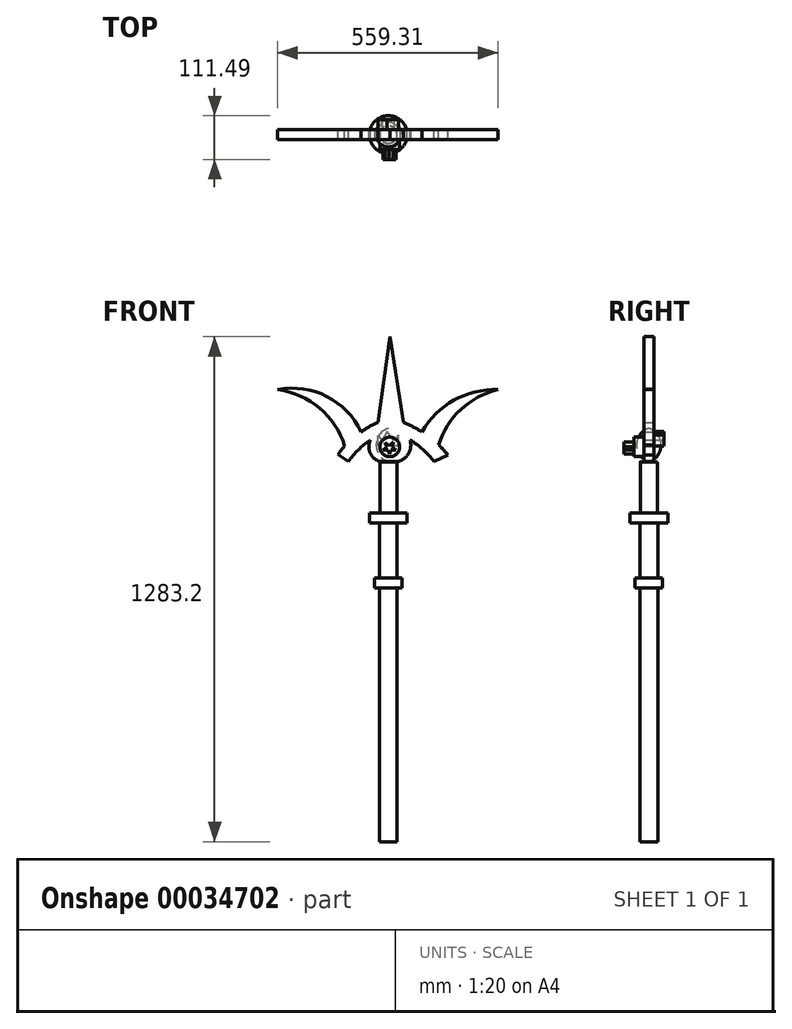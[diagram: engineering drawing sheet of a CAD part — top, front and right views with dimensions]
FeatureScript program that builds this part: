
annotation { "Feature Type Name" : "Feature", "Feature Type Description" : "" }
export const myFeature = defineFeature(function(context is Context, id is Id, definition is map)
    precondition{}
    {
        {
            var Q0;
            Q0=qCreatedBy(makeId("Front.planeOp"),FACE);
            var sketch = newSketch(context, id + "F0", { "sketchPlane" : qUnion([Q0])});
            skLineSegment(sketch, "E0.top", {"start": v(-65.68, 492.37) * mm, "end": v(-22.5, 492.37) * mm});
            skArc(sketch, "E1", {"start": v(-44.09, 492.37) * mm, "mid": v(-0.15, 503.17) * mm, "end": v(11.1, 547) * mm});
            skArc(sketch, "E2", {"start": v(-89.66, 546.65) * mm, "mid": v(-84.3, 504.88) * mm, "end": v(-44.09, 492.37) * mm});
            skArc(sketch, "E3", {"start": v(72.25, 492.37) * mm, "mid": v(20.55, 541) * mm, "end": v(-44.09, 570.32) * mm});
            skArc(sketch, "E4", {"start": v(-44.09, 570.32) * mm, "mid": v(-100.63, 538.76) * mm, "end": v(-145.8, 492.37) * mm});
            skLineSegment(sketch, "E5", {"start": v(72.25, 492.37) * mm, "end": v(107.25, 508.86) * mm});
            skLineSegment(sketch, "E6", {"start": v(-145.8, 492.37) * mm, "end": v(-171.5, 510.6) * mm});
            skArc(sketch, "E7", {"start": v(-40.37, 602.27) * mm, "mid": v(-113.68, 567.51) * mm, "end": v(-171.5, 510.6) * mm});
            skArc(sketch, "E8", {"start": v(107.25, 508.86) * mm, "mid": v(41.18, 567.81) * mm, "end": v(-40.37, 602.27) * mm});
            skArc(sketch, "E9", {"start": v(-154.84, 531.2) * mm, "mid": v(-218.84, 628.04) * mm, "end": v(-325.09, 674.82) * mm});
            skArc(sketch, "E10", {"start": v(-113.68, 567.51) * mm, "mid": v(-200.67, 658.03) * mm, "end": v(-325.09, 674.82) * mm});
            skArc(sketch, "E11", {"start": v(234.22, 674.82) * mm, "mid": v(140.25, 624.74) * mm, "end": v(83.74, 534.5) * mm});
            skArc(sketch, "E12", {"start": v(234.22, 674.82) * mm, "mid": v(122.84, 648.12) * mm, "end": v(41.18, 567.81) * mm});
            skLineSegment(sketch, "E13", {"start": v(-70.87, 591.42) * mm, "end": v(-40.37, 809.45) * mm});
            skLineSegment(sketch, "E14", {"start": v(-40.37, 809.45) * mm, "end": v(-5.06, 591.2) * mm});
            skLineSegment(sketch, "E15", {"start": v(-44.09, 492.37) * mm, "end": v(-44.09, -473.75) * mm});
            skLineSegment(sketch, "E16", {"start": v(-22.5, 492.37) * mm, "end": v(-22.5, 361.02) * mm});
            skLineSegment(sketch, "E17", {"start": v(-22.5, 361.02) * mm, "end": v(3.9, 361.02) * mm});
            skLineSegment(sketch, "E18", {"start": v(3.9, 361.02) * mm, "end": v(3.9, 335.62) * mm});
            skLineSegment(sketch, "E19", {"start": v(3.9, 335.62) * mm, "end": v(-21.5, 335.62) * mm});
            skLineSegment(sketch, "E20", {"start": v(-21.5, 335.62) * mm, "end": v(-21.5, 196.28) * mm});
            skLineSegment(sketch, "E21", {"start": v(-21.5, 196.28) * mm, "end": v(-8.8, 196.28) * mm});
            skLineSegment(sketch, "E22", {"start": v(-8.8, 196.28) * mm, "end": v(-8.8, 170.88) * mm});
            skLineSegment(sketch, "E23", {"start": v(-8.8, 170.88) * mm, "end": v(-21.5, 170.88) * mm});
            skLineSegment(sketch, "E24", {"start": v(-21.5, 170.88) * mm, "end": v(-21.5, -473.75) * mm});
            skLineSegment(sketch, "E25", {"start": v(-21.5, -473.75) * mm, "end": v(-44.09, -473.75) * mm});
            skSolve(sketch);
        }
        {
            var Q0;
            {var subQ1=sQuery(id+"F0.wireOp",EDGE,"E15");Q0=makeQuery(id+"F0.imprint","IMPRINT",FACE,{"disambiguationData":[TD([[makeQuery(id+"F0.imprint","IMPRINT",EDGE,{"derivedFrom":subQ1}),1.0]])]});}
            var Q1;
            Q1=sQuery(id+"F0.wireOp",EDGE,"E15");
            revolve(context, id + "F1", {"entities" : qUnion([Q0]), "axis" : qUnion([Q1]), "revolveType" : RevolveType.FULL});
        }
        {
            var Q0;
            {var subQ0=sQuery(id+"F0.wireOp",EDGE,"E3");var subQ3=sQuery(id+"F0.wireOp",EDGE,"E1");var subQ4=makeQuery(id+"F0.imprint","INTERSECT",VERTEX,{"derivedFrom":[subQ3,subQ0]});Q0=makeQuery(id+"F0.imprint","IMPRINT",FACE,{"disambiguationData":[TD([[makeQuery(id+"F0.imprint","IMPRINT",EDGE,{"disambiguationData":[TD([[subQ4,1.0]])],"derivedFrom":subQ3}),1.0]])]});}
            extrude(context, id + "F2", {"entities" : qUnion([Q0]), "endBound" : BoundingType.SYMMETRIC, "depth" : 25.4 * mm});
        }
        {
            var Q0;
            {var subQ1=sQuery(id+"F0.wireOp",EDGE,"E9");Q0=makeQuery(id+"F0.imprint","IMPRINT",FACE,{"disambiguationData":[TD([[makeQuery(id+"F0.imprint","IMPRINT",EDGE,{"derivedFrom":subQ1}),-1.0]])]});}
            var Q1;
            {var subQ1=sQuery(id+"F0.wireOp",EDGE,"E13");Q1=makeQuery(id+"F0.imprint","IMPRINT",FACE,{"disambiguationData":[TD([[makeQuery(id+"F0.imprint","IMPRINT",EDGE,{"derivedFrom":subQ1}),-1.0]])]});}
            var Q2;
            {var subQ0=sQuery(id+"F0.wireOp",EDGE,"E11");Q2=makeQuery(id+"F0.imprint","IMPRINT",FACE,{"disambiguationData":[TD([[makeQuery(id+"F0.imprint","IMPRINT",EDGE,{"derivedFrom":subQ0}),-1.0]])]});}
            var Q3;
            {var subQ2=sQuery(id+"F0.wireOp",EDGE,"E5");Q3=makeQuery(id+"F0.imprint","IMPRINT",FACE,{"disambiguationData":[TD([[makeQuery(id+"F0.imprint","IMPRINT",EDGE,{"derivedFrom":subQ2}),1.0]])]});}
            extrude(context, id + "F3", {"entities" : qUnion([Q0, Q1, Q2, Q3]), "operationType" : NewBodyOperationType.ADD, "endBound" : BoundingType.SYMMETRIC, "depth" : 25.4 * mm});
        }
        {
            var Q0;
            {var subQ0=sQuery(id+"F0.wireOp",EDGE,"E3");var subQ1=sQuery(id+"F0.wireOp",EDGE,"E4");Q0=makeQuery(id+"F3.boolean.opBoolean","MERGE",FACE,{"derivedFrom":[makeQuery(id+"F2.opExtrude","CAP_FACE",FACE,{"disambiguationData":[OSD([sQuery(id+"F0.wireOp",EDGE,"E0.top"),sQuery(id+"F0.wireOp",EDGE,"E1"),sQuery(id+"F0.wireOp",EDGE,"E2"),subQ0,subQ1,sQuery(id+"F0.wireOp",EDGE,"E16")])],"isStart":false}),makeQuery(id+"F3.opExtrude","CAP_FACE",FACE,{"disambiguationData":[OSD([subQ0,subQ1,sQuery(id+"F0.wireOp",EDGE,"E5"),sQuery(id+"F0.wireOp",EDGE,"E6"),sQuery(id+"F0.wireOp",EDGE,"E7"),sQuery(id+"F0.wireOp",EDGE,"E8"),sQuery(id+"F0.wireOp",EDGE,"E9"),sQuery(id+"F0.wireOp",EDGE,"E10"),sQuery(id+"F0.wireOp",EDGE,"E11"),sQuery(id+"F0.wireOp",EDGE,"E12"),sQuery(id+"F0.wireOp",EDGE,"E13"),sQuery(id+"F0.wireOp",EDGE,"E14")])],"isStart":false})]});}
            var sketch = newSketch(context, id + "F4", { "sketchPlane" : qUnion([Q0])});
            skCircle(sketch, "E26", {"center": v(-40.47, 529.52) * mm, "radius": 24.91 * mm});
            skSolve(sketch);
        }
        {
            var Q0;
            Q0 = qSketchRegion(id + "F4", true);
            extrude(context, id + "F5", {"entities" : qUnion([Q0]), "operationType" : NewBodyOperationType.ADD, "depth" : 25.4 * mm});
        }
        {
            var Q0;
            Q0=makeQuery(id+"F5.opExtrude","CAP_FACE",FACE,{"disambiguationData":[OSD([sQuery(id+"F4.wireOp",EDGE,"E26")])],"isStart":false});
            var sketch = newSketch(context, id + "F6", { "sketchPlane" : qUnion([Q0])});
            skLineSegment(sketch, "E27", {"start": v(-52.47, 541.1) * mm, "end": v(-40.88, 511.3) * mm});
            skLineSegment(sketch, "E28", {"start": v(-40.88, 511.3) * mm, "end": v(-31.37, 541.52) * mm});
            skLineSegment(sketch, "E29", {"start": v(-31.37, 541.52) * mm, "end": v(-57.44, 521.24) * mm});
            skLineSegment(sketch, "E30", {"start": v(-57.44, 521.24) * mm, "end": v(-25.16, 521.24) * mm});
            skLineSegment(sketch, "E31", {"start": v(-25.16, 521.24) * mm, "end": v(-52.47, 541.1) * mm});
            skSolve(sketch);
        }
        {
            var Q0;
            Q0 = qSketchRegion(id + "F6", true);
            extrude(context, id + "F7", {"entities" : qUnion([Q0]), "operationType" : NewBodyOperationType.ADD, "depth" : 25.4 * mm});
        }
        {
            var Q0;
            {var subQ0=sQuery(id+"F0.wireOp",EDGE,"E3");var subQ1=sQuery(id+"F0.wireOp",EDGE,"E4");Q0=makeQuery(id+"F3.boolean.opBoolean","MERGE",FACE,{"derivedFrom":[makeQuery(id+"F2.opExtrude","CAP_FACE",FACE,{"disambiguationData":[OSD([sQuery(id+"F0.wireOp",EDGE,"E0.top"),sQuery(id+"F0.wireOp",EDGE,"E1"),sQuery(id+"F0.wireOp",EDGE,"E2"),subQ0,subQ1,sQuery(id+"F0.wireOp",EDGE,"E16")])],"isStart":true}),makeQuery(id+"F3.opExtrude","CAP_FACE",FACE,{"disambiguationData":[OSD([subQ0,subQ1,sQuery(id+"F0.wireOp",EDGE,"E5"),sQuery(id+"F0.wireOp",EDGE,"E6"),sQuery(id+"F0.wireOp",EDGE,"E7"),sQuery(id+"F0.wireOp",EDGE,"E8"),sQuery(id+"F0.wireOp",EDGE,"E9"),sQuery(id+"F0.wireOp",EDGE,"E10"),sQuery(id+"F0.wireOp",EDGE,"E11"),sQuery(id+"F0.wireOp",EDGE,"E12"),sQuery(id+"F0.wireOp",EDGE,"E13"),sQuery(id+"F0.wireOp",EDGE,"E14")])],"isStart":true})]});}
            var sketch = newSketch(context, id + "F8", { "sketchPlane" : qUnion([Q0])});
            skLineSegment(sketch, "E32", {"start": v(18.45, 531.56) * mm, "end": v(18.45, 559.45) * mm});
            skLineSegment(sketch, "E33", {"start": v(18.45, 531.56) * mm, "end": v(69.95, 531.56) * mm});
            skLineSegment(sketch, "E34", {"start": v(69.95, 531.56) * mm, "end": v(69.95, 558.38) * mm});
            skLineSegment(sketch, "E35", {"start": v(69.95, 558.38) * mm, "end": v(60.3, 545.5) * mm});
            skPoint(sketch, "E35.endSnap0", {"position": v(18.45, 545.5) * mm});
            skLineSegment(sketch, "E36", {"start": v(18.45, 559.45) * mm, "end": v(30.25, 545.5) * mm});
            skLineSegment(sketch, "E37", {"start": v(30.25, 545.5) * mm, "end": v(47.42, 568.03) * mm});
            skLineSegment(sketch, "E38", {"start": v(47.42, 568.03) * mm, "end": v(60.3, 545.5) * mm});
            skSolve(sketch);
        }
        {
            var Q0;
            Q0=makeQuery(id+"F8.imprint","IMPRINT",FACE,{"disambiguationData":[TD([[makeQuery(id+"F8.imprint","IMPRINT",EDGE,{"derivedFrom":sQuery(id+"F8.wireOp",EDGE,"E32")}),-1.0]])]});
            extrude(context, id + "F9", {"entities" : qUnion([Q0]), "operationType" : NewBodyOperationType.ADD, "depth" : 25.4 * mm});
        }
    });
